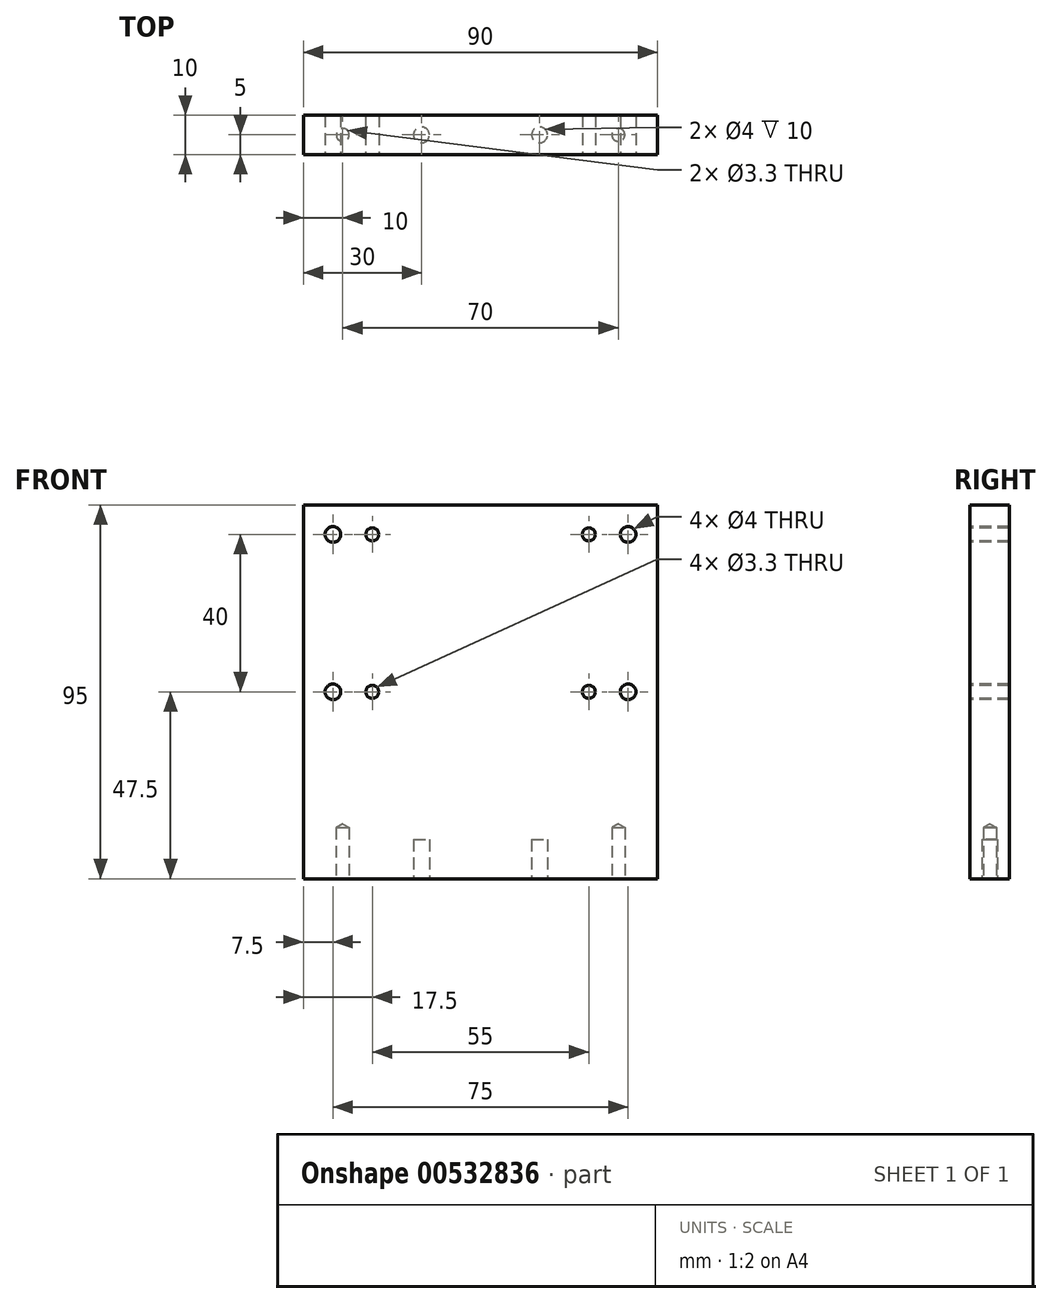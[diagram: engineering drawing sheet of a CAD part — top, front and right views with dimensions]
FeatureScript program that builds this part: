
annotation { "Feature Type Name" : "Feature", "Feature Type Description" : "" }
export const myFeature = defineFeature(function(context is Context, id is Id, definition is map)
    precondition{}
    {
        {
            var Q0;
            Q0=qCreatedBy(makeId("Top.planeOp"),FACE);
            var sketch = newSketch(context, id + "F0", { "sketchPlane" : qUnion([Q0])});
            skLineSegment(sketch, "E0.bottom", {"start": v(-45, 5) * mm, "end": v(45, 5) * mm});
            skLineSegment(sketch, "E0.top", {"start": v(-45, -5) * mm, "end": v(45, -5) * mm});
            skLineSegment(sketch, "E0.left", {"start": v(-45, 5) * mm, "end": v(-45, -5) * mm});
            skLineSegment(sketch, "E0.right", {"start": v(45, 5) * mm, "end": v(45, -5) * mm});
            skSolve(sketch);
        }
        {
            var Q0;
            Q0 = qSketchRegion(id + "F0", true);
            extrude(context, id + "F1", {"entities" : qUnion([Q0]), "depth" : 95 * mm, "offsetDistance" : 25 * mm});
        }
        {
            var Q0;
            Q0=makeQuery(id+"F1.opExtrude","CAP_FACE",FACE,{"disambiguationData":[OSD([sQuery(id+"F0.wireOp",EDGE,"E0.bottom"),sQuery(id+"F0.wireOp",EDGE,"E0.top"),sQuery(id+"F0.wireOp",EDGE,"E0.left"),sQuery(id+"F0.wireOp",EDGE,"E0.right")])],"isStart":true});
            var sketch = newSketch(context, id + "F2", { "sketchPlane" : qUnion([Q0])});
            skCircle(sketch, "E1", {"center": v(-15, 0) * mm, "radius": 2 * mm});
            skCircle(sketch, "E2", {"center": v(15, 0) * mm, "radius": 2 * mm});
            skPoint(sketch, "E3", {"position": v(-35, 0) * mm});
            skPoint(sketch, "E4", {"position": v(35, 0) * mm});
            skSolve(sketch);
        }
        {
            var Q0;
            Q0=makeQuery(id+"F2.imprint","IMPRINT",FACE,{"disambiguationData":[TD([[makeQuery(id+"F2.imprint","IMPRINT",EDGE,{"derivedFrom":sQuery(id+"F2.wireOp",EDGE,"E1")}),1.0]])]});
            var Q1;
            Q1=makeQuery(id+"F2.imprint","IMPRINT",FACE,{"disambiguationData":[TD([[makeQuery(id+"F2.imprint","IMPRINT",EDGE,{"derivedFrom":sQuery(id+"F2.wireOp",EDGE,"E2")}),1.0]])]});
            extrude(context, id + "F3", {"entities" : qUnion([Q0, Q1]), "operationType" : NewBodyOperationType.REMOVE, "oppositeDirection" : true, "depth" : 10 * mm, "offsetDistance" : 25 * mm});
        }
        {
            var Q0;
            Q0=sQuery(id+"F2.wireOp",VERTEX,"E3");
            var Q1;
            Q1=sQuery(id+"F2.wireOp",VERTEX,"E4");
            var Q2;
            Q2=makeQuery(id+"F1.opExtrude","SWEPT_BODY",BODY,{"disambiguationData":[OSD([sQuery(id+"F0.wireOp",EDGE,"E0.bottom"),sQuery(id+"F0.wireOp",EDGE,"E0.top"),sQuery(id+"F0.wireOp",EDGE,"E0.left"),sQuery(id+"F0.wireOp",EDGE,"E0.right")])]});
            hole(context, id + "F4", {"style" : HoleStyle.SIMPLE, "endStyle" : HoleEndStyle.BLIND, "standardTappedOrClearance" : lookupTablePath({ "standard" : "ISO", "engagement" : "75%", "pitch" : "0.7 mm", "size" : "M4", "type" : "Tapped" }), "standardBlindInLast" : lookupTablePath({ "standard" : "ISO", "engagement" : "75%", "pitch" : "0.7 mm", "size" : "M4", "type" : "Tapped" }), "holeDiameter" : 3.3 * mm, "showTappedDepth" : true, "holeDepth" : 13 * mm, "tappedDepth" : 10.9 * mm, "tapClearance" : 3, "locations" : qUnion([Q0, Q1]), "scope" : qUnion([Q2]), "majorDiameter" : 4 * mm});
        }
        {
            var Q0;
            Q0=makeQuery(id+"F1.opExtrude","SWEPT_FACE",FACE,{"disambiguationData":[OSD([sQuery(id+"F0.wireOp",EDGE,"E0.top")])]});
            var sketch = newSketch(context, id + "F5", { "sketchPlane" : qUnion([Q0])});
            skPoint(sketch, "E5", {"position": v(-37.5, 87.5) * mm});
            skPoint(sketch, "E6", {"position": v(-27.5, 87.5) * mm});
            skPoint(sketch, "E7", {"position": v(27.5, 87.5) * mm});
            skPoint(sketch, "E8", {"position": v(37.5, 87.5) * mm});
            skPoint(sketch, "E9", {"position": v(-37.5, 47.5) * mm});
            skPoint(sketch, "E10", {"position": v(-27.5, 47.5) * mm});
            skPoint(sketch, "E11", {"position": v(27.5, 47.5) * mm});
            skPoint(sketch, "E12", {"position": v(37.5, 47.5) * mm});
            skCircle(sketch, "E13", {"center": v(-37.5, 87.5) * mm, "radius": 2 * mm});
            skCircle(sketch, "E14", {"center": v(-37.5, 47.5) * mm, "radius": 2 * mm});
            skCircle(sketch, "E15", {"center": v(37.5, 47.5) * mm, "radius": 2 * mm});
            skCircle(sketch, "E16", {"center": v(37.5, 87.5) * mm, "radius": 2 * mm});
            skSolve(sketch);
        }
        {
            var Q0;
            Q0=makeQuery(id+"F5.imprint","IMPRINT",FACE,{"disambiguationData":[TD([[makeQuery(id+"F5.imprint","IMPRINT",EDGE,{"derivedFrom":sQuery(id+"F5.wireOp",EDGE,"E14")}),1.0]])]});
            var Q1;
            Q1=makeQuery(id+"F5.imprint","IMPRINT",FACE,{"disambiguationData":[TD([[makeQuery(id+"F5.imprint","IMPRINT",EDGE,{"derivedFrom":sQuery(id+"F5.wireOp",EDGE,"E13")}),1.0]])]});
            var Q2;
            Q2=makeQuery(id+"F5.imprint","IMPRINT",FACE,{"disambiguationData":[TD([[makeQuery(id+"F5.imprint","IMPRINT",EDGE,{"derivedFrom":sQuery(id+"F5.wireOp",EDGE,"E16")}),1.0]])]});
            var Q3;
            Q3=makeQuery(id+"F5.imprint","IMPRINT",FACE,{"disambiguationData":[TD([[makeQuery(id+"F5.imprint","IMPRINT",EDGE,{"derivedFrom":sQuery(id+"F5.wireOp",EDGE,"E15")}),1.0]])]});
            extrude(context, id + "F6", {"entities" : qUnion([Q0, Q1, Q2, Q3]), "operationType" : NewBodyOperationType.REMOVE, "endBound" : BoundingType.THROUGH_ALL, "oppositeDirection" : true, "depth" : 25 * mm, "offsetDistance" : 25 * mm});
        }
        {
            var Q0;
            Q0=sQuery(id+"F5.wireOp",VERTEX,"E10");
            var Q1;
            Q1=sQuery(id+"F5.wireOp",VERTEX,"E6");
            var Q2;
            Q2=sQuery(id+"F5.wireOp",VERTEX,"E7");
            var Q3;
            Q3=sQuery(id+"F5.wireOp",VERTEX,"E11");
            var Q4;
            Q4=makeQuery(id+"F1.opExtrude","SWEPT_BODY",BODY,{"disambiguationData":[OSD([sQuery(id+"F0.wireOp",EDGE,"E0.bottom"),sQuery(id+"F0.wireOp",EDGE,"E0.top"),sQuery(id+"F0.wireOp",EDGE,"E0.left"),sQuery(id+"F0.wireOp",EDGE,"E0.right")])]});
            hole(context, id + "F7", {"style" : HoleStyle.SIMPLE, "endStyle" : HoleEndStyle.THROUGH, "standardTappedOrClearance" : lookupTablePath({ "standard" : "ISO", "engagement" : "75%", "pitch" : "0.7 mm", "size" : "M4", "type" : "Tapped" }), "standardBlindInLast" : lookupTablePath({ "standard" : "ISO", "engagement" : "75%", "pitch" : "0.7 mm", "size" : "M4", "type" : "Tapped" }), "holeDiameter" : 3.3 * mm, "showTappedDepth" : true, "isTappedThrough" : true, "tappedDepth" : 10.9 * mm, "tapClearance" : 3, "locations" : qUnion([Q0, Q1, Q2, Q3]), "scope" : qUnion([Q4]), "majorDiameter" : 4 * mm});
        }
    });
